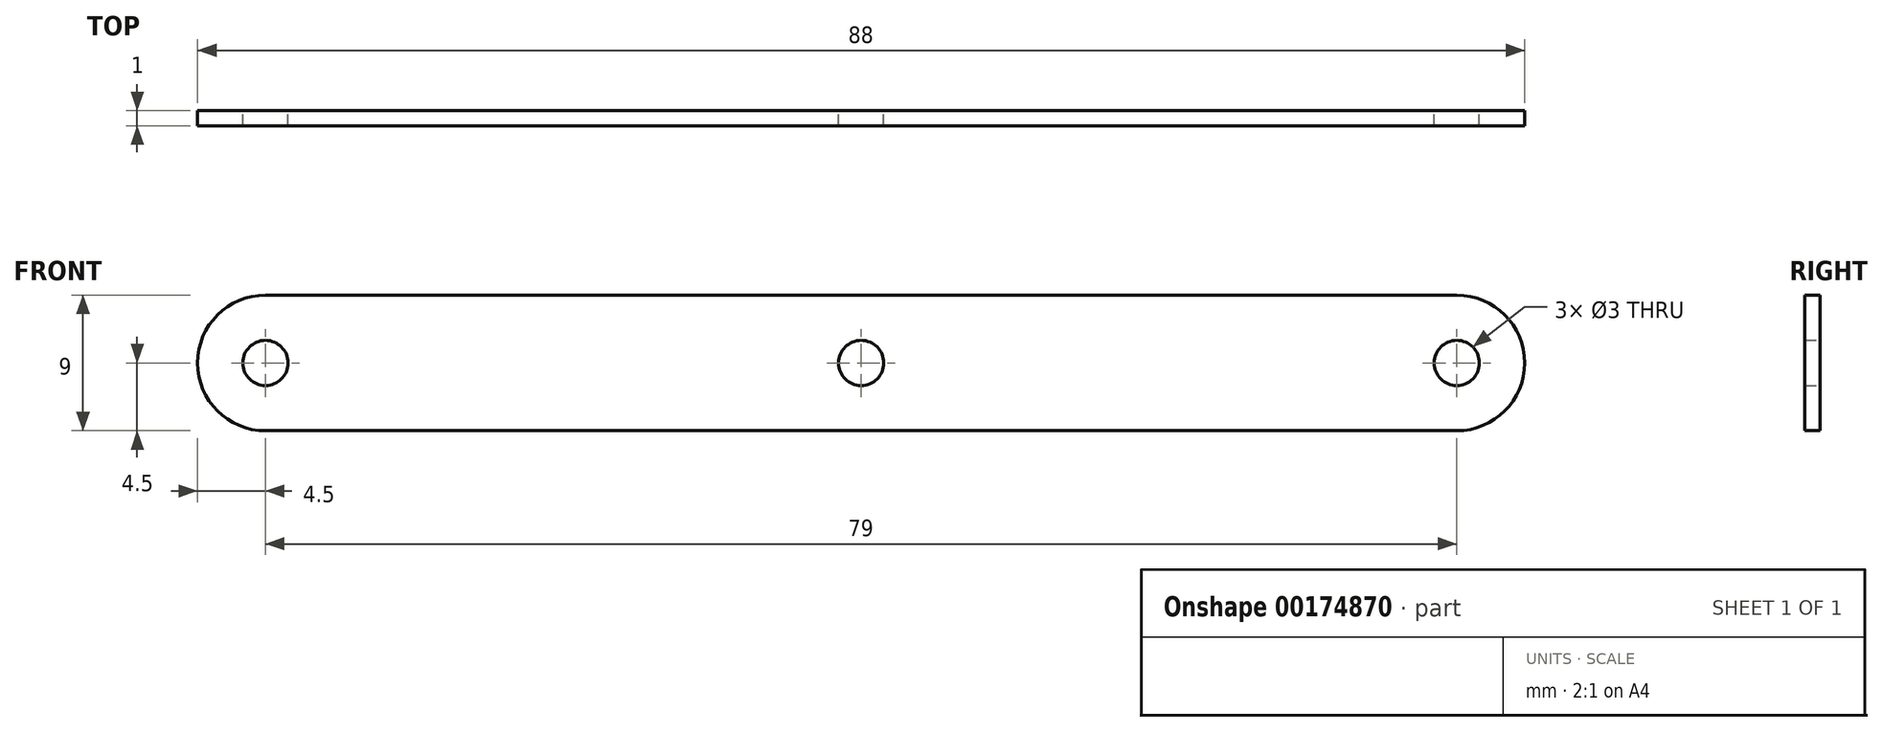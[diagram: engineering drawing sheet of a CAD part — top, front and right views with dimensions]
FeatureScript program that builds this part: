
annotation { "Feature Type Name" : "Feature", "Feature Type Description" : "" }
export const myFeature = defineFeature(function(context is Context, id is Id, definition is map)
    precondition{}
    {
        {
            var Q0;
            Q0=qCreatedBy(makeId("Front.planeOp"),FACE);
            var sketch = newSketch(context, id + "F0", { "sketchPlane" : qUnion([Q0])});
            skLineSegment(sketch, "E0.bottom", {"start": v(39.5, 4.5) * mm, "end": v(-39.5, 4.5) * mm});
            skLineSegment(sketch, "E0.top", {"start": v(39.5, -4.5) * mm, "end": v(-39.5, -4.5) * mm});
            skPoint(sketch, "E0.middle", {"position": v(0, 0) * mm});
            skCircle(sketch, "E1", {"center": v(39.5, 0) * mm, "radius": 1.5 * mm});
            skCircle(sketch, "E2", {"center": v(-39.5, 0) * mm, "radius": 1.5 * mm});
            skCircle(sketch, "E3", {"center": v(-39.5, 0) * mm, "radius": 4.5 * mm});
            skCircle(sketch, "E4", {"center": v(39.5, 0) * mm, "radius": 4.5 * mm});
            skPoint(sketch, "E0.right.start.orphan", {"position": v(-50, 4.5) * mm});
            skPoint(sketch, "E5.orphan", {"position": v(-41, -4.5) * mm});
            skPoint(sketch, "E0.left.start.orphan", {"position": v(41, 4.5) * mm});
            skPoint(sketch, "E6.orphan", {"position": v(50, -4.5) * mm});
            skCircle(sketch, "E7", {"center": v(0, 0) * mm, "radius": 1.5 * mm});
            skSolve(sketch);
        }
        {
            var Q0;
            Q0 = qSketchRegion(id + "F0", true);
            extrude(context, id + "F1", {"entities" : qUnion([Q0]), "depth" : 1 * mm});
        }
    });
